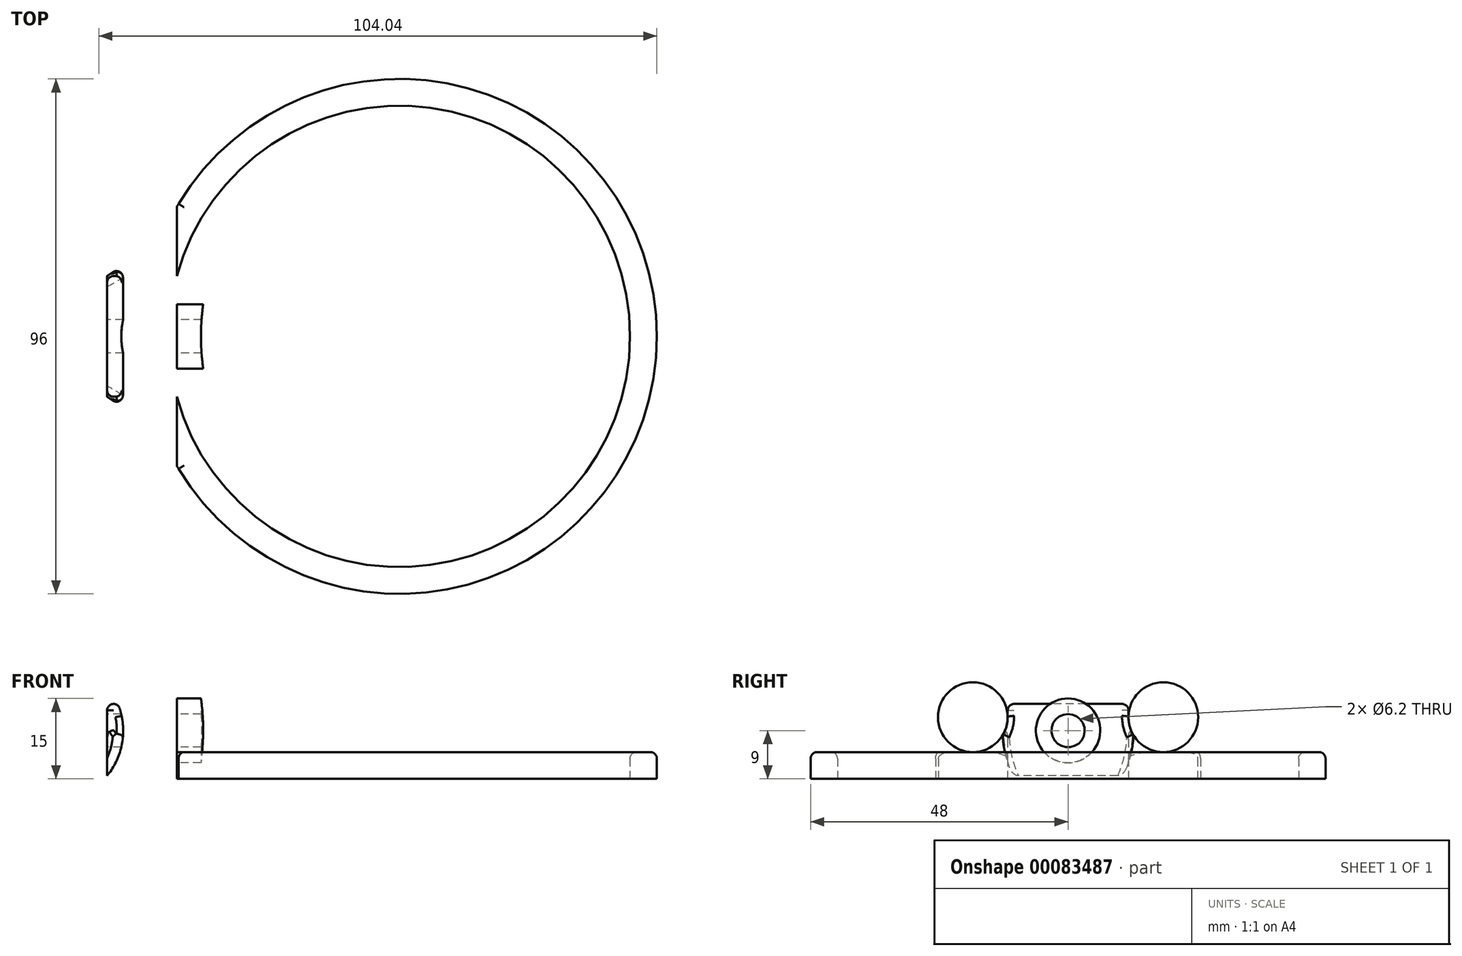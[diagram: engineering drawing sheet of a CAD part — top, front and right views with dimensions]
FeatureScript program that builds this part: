
annotation { "Feature Type Name" : "Feature", "Feature Type Description" : "" }
export const myFeature = defineFeature(function(context is Context, id is Id, definition is map)
    precondition{}
    {
        {
            var Q0;
            Q0=qCreatedBy(makeId("Top.planeOp"),FACE);
            var sketch = newSketch(context, id + "F0", { "sketchPlane" : qUnion([Q0])});
            skCircle(sketch, "E0", {"center": v(0, 0) * mm, "radius": 43 * mm});
            skCircle(sketch, "E1", {"center": v(0, 0) * mm, "radius": 48 * mm});
            skLineSegment(sketch, "E2.bottom", {"start": v(-41.5, -11.26) * mm, "end": v(-54.5, -11.26) * mm});
            skLineSegment(sketch, "E2.top", {"start": v(-41.5, 11.26) * mm, "end": v(-54.5, 11.26) * mm});
            skLineSegment(sketch, "E2.left", {"start": v(-41.5, -11.26) * mm, "end": v(-41.5, 11.26) * mm});
            skLineSegment(sketch, "E2.right", {"start": v(-54.5, -11.26) * mm, "end": v(-54.5, 11.26) * mm});
            skPoint(sketch, "E2.middle", {"position": v(-48, 0) * mm});
            skArc(sketch, "E3", {"start": v(-54.5, 11.26) * mm, "mid": v(-47.1, 17.26) * mm, "end": v(-41.16, 24.7) * mm});
            skArc(sketch, "E4.MirrorCS", {"start": v(-54.5, -11.26) * mm, "mid": v(-47.1, -17.26) * mm, "end": v(-41.16, -24.7) * mm});
            skSolve(sketch);
        }
        {
            var Q0;
            {var subQ0=sQuery(id+"F0.wireOp",EDGE,"E3");var subQ1=sQuery(id+"F0.wireOp",EDGE,"E1");var subQ8=makeQuery(id+"F0.imprint","INTERSECT",VERTEX,{"disambiguationData":[OD(1.0)],"derivedFrom":[subQ1,subQ0]});Q0=makeQuery(id+"F0.imprint","IMPRINT",FACE,{"disambiguationData":[TD([[makeQuery(id+"F0.imprint","IMPRINT",EDGE,{"disambiguationData":[TD([[subQ8,-1.0]])],"derivedFrom":subQ1}),1.0]])]});}
            var Q1;
            {var subQ4=sQuery(id+"F0.wireOp",EDGE,"E2.top");var subQ6=sQuery(id+"F0.wireOp",EDGE,"E1");var subQ7=makeQuery(id+"F0.imprint","INTERSECT",VERTEX,{"derivedFrom":[subQ6,subQ4]});Q1=makeQuery(id+"F0.imprint","IMPRINT",FACE,{"disambiguationData":[TD([[makeQuery(id+"F0.imprint","IMPRINT",EDGE,{"disambiguationData":[TD([[subQ7,-1.0]])],"derivedFrom":subQ6}),1.0]])]});}
            var Q2;
            {var subQ0=sQuery(id+"F0.wireOp",EDGE,"E3");var subQ1=sQuery(id+"F0.wireOp",EDGE,"E1");var subQ2=makeQuery(id+"F0.imprint","INTERSECT",VERTEX,{"disambiguationData":[OD(1.0)],"derivedFrom":[subQ1,subQ0]});Q2=makeQuery(id+"F0.imprint","IMPRINT",FACE,{"disambiguationData":[TD([[makeQuery(id+"F0.imprint","IMPRINT",EDGE,{"disambiguationData":[TD([[subQ2,-1.0]])],"derivedFrom":subQ1}),-1.0]])]});}
            var Q3;
            {var subQ5=sQuery(id+"F0.wireOp",EDGE,"E2.right");Q3=makeQuery(id+"F0.imprint","IMPRINT",FACE,{"disambiguationData":[TD([[makeQuery(id+"F0.imprint","IMPRINT",EDGE,{"derivedFrom":subQ5}),-1.0]])]});}
            var Q4;
            {var subQ0=sQuery(id+"F0.wireOp",EDGE,"E4.MirrorCS");var subQ1=sQuery(id+"F0.wireOp",EDGE,"E1");var subQ2=makeQuery(id+"F0.imprint","INTERSECT",VERTEX,{"disambiguationData":[OD(1.0)],"derivedFrom":[subQ1,subQ0]});Q4=makeQuery(id+"F0.imprint","IMPRINT",FACE,{"disambiguationData":[TD([[makeQuery(id+"F0.imprint","IMPRINT",EDGE,{"disambiguationData":[TD([[subQ2,1.0]])],"derivedFrom":subQ1}),-1.0]])]});}
            extrude(context, id + "F1", {"entities" : qUnion([Q0, Q1, Q2, Q3, Q4]), "depth" : 5 * mm});
        }
        {
            var Q0;
            {var subQ5=sQuery(id+"F0.wireOp",EDGE,"E2.right");Q0=makeQuery(id+"F0.imprint","IMPRINT",FACE,{"disambiguationData":[TD([[makeQuery(id+"F0.imprint","IMPRINT",EDGE,{"derivedFrom":subQ5}),-1.0]])]});}
            var Q1;
            {var subQ4=sQuery(id+"F0.wireOp",EDGE,"E2.top");var subQ6=sQuery(id+"F0.wireOp",EDGE,"E1");var subQ7=makeQuery(id+"F0.imprint","INTERSECT",VERTEX,{"derivedFrom":[subQ6,subQ4]});Q1=makeQuery(id+"F0.imprint","IMPRINT",FACE,{"disambiguationData":[TD([[makeQuery(id+"F0.imprint","IMPRINT",EDGE,{"disambiguationData":[TD([[subQ7,-1.0]])],"derivedFrom":subQ6}),1.0]])]});}
            extrude(context, id + "F2", {"entities" : qUnion([Q0, Q1]), "operationType" : NewBodyOperationType.ADD, "depth" : 18 * mm});
        }
        {
            var Q0;
            {var subQ0=sQuery(id+"F0.wireOp",EDGE,"E2.right");Q0=makeQuery(id+"F2.boolean.opBoolean","MERGE",FACE,{"derivedFrom":[makeQuery(id+"F1.opExtrude","SWEPT_FACE",FACE,{"disambiguationData":[OSD([subQ0])]}),makeQuery(id+"F2.opExtrude","SWEPT_FACE",FACE,{"disambiguationData":[OSD([subQ0])]})]});}
            var sketch = newSketch(context, id + "F3", { "sketchPlane" : qUnion([Q0])});
            skLineSegment(sketch, "E5", {"start": v(0, 18) * mm, "end": v(0, 0) * mm, "construction": true});
            skPoint(sketch, "E5.startSnap0", {"position": v(0, 18) * mm});
            skLineSegment(sketch, "E6.bottom", {"start": v(-11.26, 18) * mm, "end": v(11.26, 18) * mm});
            skLineSegment(sketch, "E6.top", {"start": v(-11.26, 0) * mm, "end": v(11.26, 0) * mm});
            skLineSegment(sketch, "E6.left", {"start": v(-11.26, 18) * mm, "end": v(-11.26, 0) * mm});
            skLineSegment(sketch, "E6.right", {"start": v(11.26, 18) * mm, "end": v(11.26, 0) * mm});
            skPoint(sketch, "E7", {"position": v(-11.26, 9) * mm});
            skCircle(sketch, "E8", {"center": v(0, 9) * mm, "radius": 6 * mm});
            skCircle(sketch, "E9", {"center": v(0, 9) * mm, "radius": 3.1 * mm});
            skSolve(sketch);
        }
        {
            var Q0;
            Q0=makeQuery(id+"F3.imprint","IMPRINT",FACE,{"disambiguationData":[TD([[makeQuery(id+"F3.imprint","IMPRINT",EDGE,{"derivedFrom":sQuery(id+"F3.wireOp",EDGE,"E9")}),1.0]])]});
            extrude(context, id + "F4", {"entities" : qUnion([Q0]), "operationType" : NewBodyOperationType.REMOVE, "endBound" : BoundingType.THROUGH_ALL, "oppositeDirection" : true, "depth" : 9.76 * mm});
        }
        {
            var Q0;
            Q0=makeQuery(id+"F3.imprint","IMPRINT",FACE,{"disambiguationData":[TD([[makeQuery(id+"F3.imprint","IMPRINT",EDGE,{"derivedFrom":sQuery(id+"F3.wireOp",EDGE,"E8")}),1.0]])]});
            var Q1;
            {var subQ0=sQuery(id+"F0.wireOp",EDGE,"E0");Q1=makeQuery(id+"F2.boolean.opBoolean","MERGE",FACE,{"derivedFrom":[makeQuery(id+"F1.opExtrude","SWEPT_FACE",FACE,{"disambiguationData":[OSD([subQ0])]}),makeQuery(id+"F2.opExtrude","SWEPT_FACE",FACE,{"disambiguationData":[OSD([subQ0])]})]});}
            extrude(context, id + "F5", {"entities" : qUnion([Q0]), "endBound" : BoundingType.UP_TO_SURFACE, "oppositeDirection" : true, "endBoundEntityFace" : qUnion([Q1]), "depth" : 15 * mm, "hasSecondDirectionDraft" : true, "secondDirectionDraftAngle" : 3 * degree});
        }
        {
            var Q0;
            Q0=makeQuery(id+"F5.opExtrude","SWEPT_BODY",BODY,{"disambiguationData":[OSD([sQuery(id+"F3.wireOp",EDGE,"E8"),sQuery(id+"F3.wireOp",EDGE,"E9")])]});
            transform(context, id + "F6", {"entities" : qUnion([Q0]), "transformType" : TransformType.TRANSLATION_3D, "dx" : 6 * mm, "dy" : 0 * mm, "dz" : 0 * mm, "makeCopy" : false});
        }
        {
            var Q0;
            Q0=makeQuery(id+"F5.opExtrude","SWEPT_BODY",BODY,{"disambiguationData":[OSD([sQuery(id+"F3.wireOp",EDGE,"E8"),sQuery(id+"F3.wireOp",EDGE,"E9")])]});
            var Q1;
            Q1=makeQuery(id+"F1.opExtrude","SWEPT_BODY",BODY,{"disambiguationData":[OSD([sQuery(id+"F0.wireOp",EDGE,"E0"),sQuery(id+"F0.wireOp",EDGE,"E1"),sQuery(id+"F0.wireOp",EDGE,"E2.right"),sQuery(id+"F0.wireOp",EDGE,"E3"),sQuery(id+"F0.wireOp",EDGE,"E4.MirrorCS")])]});
            booleanBodies(context, id + "F7", {"operationType" : BooleanOperationType.SUBTRACTION, "tools" : qUnion([Q0]), "targets" : qUnion([Q1]), "keepTools" : true});
        }
        {
            var Q0;
            Q0=makeQuery(id+"F2.opExtrude","SWEPT_FACE",FACE,{"disambiguationData":[OSD([sQuery(id+"F0.wireOp",EDGE,"E2.bottom")])]});
            var sketch = newSketch(context, id + "F8", { "sketchPlane" : qUnion([Q0])});
            skLineSegment(sketch, "E10.bottom", {"start": v(-54.5, 18) * mm, "end": v(-41.5, 18) * mm});
            skLineSegment(sketch, "E10.top", {"start": v(-54.5, 0) * mm, "end": v(-41.5, 0) * mm});
            skLineSegment(sketch, "E10.left", {"start": v(-54.5, 18) * mm, "end": v(-54.5, 0) * mm});
            skLineSegment(sketch, "E10.right", {"start": v(-41.5, 18) * mm, "end": v(-41.5, 0) * mm});
            skCircle(sketch, "E11", {"center": v(-64.85, 9) * mm, "radius": 13.35 * mm});
            skPoint(sketch, "E12", {"position": v(-54.5, 9) * mm});
            skLineSegment(sketch, "E13.0.0", {"start": v(-48.5, 15) * mm, "end": v(-48.5, 3) * mm});
            skSolve(sketch);
        }
        {
            var Q0;
            {var subQ0=sQuery(id+"F8.wireOp",EDGE,"E10.left");var subQ3=sQuery(id+"F8.wireOp",EDGE,"E11");var subQ4=makeQuery(id+"F8.imprint","INTERSECT",VERTEX,{"disambiguationData":[OD(0.0)],"derivedFrom":[subQ0,subQ3]});Q0=makeQuery(id+"F8.imprint","IMPRINT",FACE,{"disambiguationData":[TD([[makeQuery(id+"F8.imprint","IMPRINT",EDGE,{"disambiguationData":[TD([[subQ4,-1.0]])],"derivedFrom":subQ0}),1.0]])]});}
            var Q1;
            {var subQ0=sQuery(id+"F8.wireOp",EDGE,"E10.left");var subQ3=sQuery(id+"F8.wireOp",EDGE,"E11");var subQ4=makeQuery(id+"F8.imprint","INTERSECT",VERTEX,{"disambiguationData":[OD(1.0)],"derivedFrom":[subQ0,subQ3]});Q1=makeQuery(id+"F8.imprint","IMPRINT",FACE,{"disambiguationData":[TD([[makeQuery(id+"F8.imprint","IMPRINT",EDGE,{"disambiguationData":[TD([[subQ4,1.0]])],"derivedFrom":subQ0}),1.0]])]});}
            var Q2;
            Q2=sQuery(id+"F8.wireOp",EDGE,"E11");
            extrude(context, id + "F9", {"entities" : qUnion([Q0, Q1]), "operationType" : NewBodyOperationType.REMOVE, "surfaceEntities" : qUnion([Q2]), "endBound" : BoundingType.THROUGH_ALL, "oppositeDirection" : true, "depth" : 25 * mm, "hasSecondDirection" : true, "secondDirectionBound" : SecondDirectionBoundingType.THROUGH_ALL, "secondDirectionOppositeDirection" : false, "secondDirectionDepth" : 25 * mm});
        }
        {
            var Q0;
            Q0=makeQuery(id+"F2.boolean.opBoolean","INTERSECT",EDGE,{"derivedFrom":[makeQuery(id+"F1.opExtrude","CAP_FACE",FACE,{"disambiguationData":[OSD([sQuery(id+"F0.wireOp",EDGE,"E0"),sQuery(id+"F0.wireOp",EDGE,"E1"),sQuery(id+"F0.wireOp",EDGE,"E2.right"),sQuery(id+"F0.wireOp",EDGE,"E3"),sQuery(id+"F0.wireOp",EDGE,"E4.MirrorCS")])],"isStart":false}),makeQuery(id+"F2.opExtrude","SWEPT_FACE",FACE,{"disambiguationData":[OSD([sQuery(id+"F0.wireOp",EDGE,"E2.bottom")])]})]});
            var Q1;
            Q1=makeQuery(id+"F2.opExtrude","CAP_EDGE",EDGE,{"disambiguationData":[OSD([sQuery(id+"F0.wireOp",EDGE,"E2.bottom")])],"isStart":false});
            var Q2;
            Q2=makeQuery(id+"F2.boolean.opBoolean","INTERSECT",EDGE,{"derivedFrom":[makeQuery(id+"F1.opExtrude","CAP_FACE",FACE,{"disambiguationData":[OSD([sQuery(id+"F0.wireOp",EDGE,"E0"),sQuery(id+"F0.wireOp",EDGE,"E1"),sQuery(id+"F0.wireOp",EDGE,"E2.right"),sQuery(id+"F0.wireOp",EDGE,"E3"),sQuery(id+"F0.wireOp",EDGE,"E4.MirrorCS")])],"isStart":false}),makeQuery(id+"F2.opExtrude","SWEPT_FACE",FACE,{"disambiguationData":[OSD([sQuery(id+"F0.wireOp",EDGE,"E2.top")])]})]});
            var Q3;
            Q3=makeQuery(id+"F2.opExtrude","CAP_EDGE",EDGE,{"disambiguationData":[OSD([sQuery(id+"F0.wireOp",EDGE,"E2.top")])],"isStart":false});
            fillet(context, id + "F10", {"entities" : qUnion([Q0, Q1, Q2, Q3]), "radius" : 6.5 * mm, "tangentPropagation" : true, "allowEdgeOverflow" : false});
        }
        {
            var Q0;
            Q0=makeQuery(id+"F1.opExtrude","CAP_EDGE",EDGE,{"disambiguationData":[OSD([sQuery(id+"F0.wireOp",EDGE,"E0")])],"isStart":false});
            var Q1;
            Q1=makeQuery(id+"F1.opExtrude","CAP_EDGE",EDGE,{"disambiguationData":[OSD([sQuery(id+"F0.wireOp",EDGE,"E1")])],"isStart":false});
            var Q2;
            Q2=makeQuery(id+"F1.opExtrude","CAP_EDGE",EDGE,{"disambiguationData":[OSD([sQuery(id+"F0.wireOp",EDGE,"E4.MirrorCS")])],"isStart":false});
            var Q3;
            {var subQ0=sQuery(id+"F0.wireOp",EDGE,"E4.MirrorCS");Q3=makeQuery(id+"F10.opFillet","BLEND_EDGE",EDGE,{"blendedFrom":[makeQuery(id+"F2.boolean.opBoolean","INTERSECT",EDGE,{"derivedFrom":[makeQuery(id+"F1.opExtrude","CAP_FACE",FACE,{"disambiguationData":[OSD([sQuery(id+"F0.wireOp",EDGE,"E0"),sQuery(id+"F0.wireOp",EDGE,"E1"),sQuery(id+"F0.wireOp",EDGE,"E2.right"),sQuery(id+"F0.wireOp",EDGE,"E3"),subQ0])],"isStart":false}),makeQuery(id+"F2.opExtrude","SWEPT_FACE",FACE,{"disambiguationData":[OSD([sQuery(id+"F0.wireOp",EDGE,"E2.bottom")])]})]}),makeQuery(id+"F1.opExtrude","SWEPT_FACE",FACE,{"disambiguationData":[OSD([subQ0])]})],"blendedInto":[makeQuery(id+"F1.opExtrude","SWEPT_FACE",FACE,{"disambiguationData":[OSD([subQ0])]})]});}
            var Q4;
            {var subQ0=sQuery(id+"F0.wireOp",EDGE,"E0");Q4=makeQuery(id+"F10.opFillet","BLEND_EDGE",EDGE,{"blendedFrom":[makeQuery(id+"F2.boolean.opBoolean","INTERSECT",EDGE,{"derivedFrom":[makeQuery(id+"F1.opExtrude","CAP_FACE",FACE,{"disambiguationData":[OSD([subQ0,sQuery(id+"F0.wireOp",EDGE,"E1"),sQuery(id+"F0.wireOp",EDGE,"E2.right"),sQuery(id+"F0.wireOp",EDGE,"E3"),sQuery(id+"F0.wireOp",EDGE,"E4.MirrorCS")])],"isStart":false}),makeQuery(id+"F2.opExtrude","SWEPT_FACE",FACE,{"disambiguationData":[OSD([sQuery(id+"F0.wireOp",EDGE,"E2.bottom")])]})]}),makeQuery(id+"F2.boolean.opBoolean","MERGE",FACE,{"derivedFrom":[makeQuery(id+"F1.opExtrude","SWEPT_FACE",FACE,{"disambiguationData":[OSD([subQ0])]}),makeQuery(id+"F2.opExtrude","SWEPT_FACE",FACE,{"disambiguationData":[OSD([subQ0])]})]})],"blendedInto":[makeQuery(id+"F2.boolean.opBoolean","MERGE",FACE,{"derivedFrom":[makeQuery(id+"F1.opExtrude","SWEPT_FACE",FACE,{"disambiguationData":[OSD([subQ0])]}),makeQuery(id+"F2.opExtrude","SWEPT_FACE",FACE,{"disambiguationData":[OSD([subQ0])]})]})]});}
            var Q5;
            {var subQ0=sQuery(id+"F0.wireOp",EDGE,"E0");Q5=makeQuery(id+"F10.opFillet","BLEND_EDGE",EDGE,{"blendedFrom":[makeQuery(id+"F2.opExtrude","CAP_EDGE",EDGE,{"disambiguationData":[OSD([sQuery(id+"F0.wireOp",EDGE,"E2.bottom")])],"isStart":false}),makeQuery(id+"F2.boolean.opBoolean","MERGE",FACE,{"derivedFrom":[makeQuery(id+"F1.opExtrude","SWEPT_FACE",FACE,{"disambiguationData":[OSD([subQ0])]}),makeQuery(id+"F2.opExtrude","SWEPT_FACE",FACE,{"disambiguationData":[OSD([subQ0])]})]})],"blendedInto":[makeQuery(id+"F2.boolean.opBoolean","MERGE",FACE,{"derivedFrom":[makeQuery(id+"F1.opExtrude","SWEPT_FACE",FACE,{"disambiguationData":[OSD([subQ0])]}),makeQuery(id+"F2.opExtrude","SWEPT_FACE",FACE,{"disambiguationData":[OSD([subQ0])]})]})]});}
            var Q6;
            Q6=makeQuery(id+"F2.opExtrude","CAP_EDGE",EDGE,{"disambiguationData":[OSD([sQuery(id+"F0.wireOp",EDGE,"E0")])],"isStart":false});
            var Q7;
            {var subQ0=sQuery(id+"F0.wireOp",EDGE,"E0");Q7=makeQuery(id+"F10.opFillet","BLEND_EDGE",EDGE,{"blendedFrom":[makeQuery(id+"F2.opExtrude","CAP_EDGE",EDGE,{"disambiguationData":[OSD([sQuery(id+"F0.wireOp",EDGE,"E2.top")])],"isStart":false}),makeQuery(id+"F2.boolean.opBoolean","MERGE",FACE,{"derivedFrom":[makeQuery(id+"F1.opExtrude","SWEPT_FACE",FACE,{"disambiguationData":[OSD([subQ0])]}),makeQuery(id+"F2.opExtrude","SWEPT_FACE",FACE,{"disambiguationData":[OSD([subQ0])]})]})],"blendedInto":[makeQuery(id+"F2.boolean.opBoolean","MERGE",FACE,{"derivedFrom":[makeQuery(id+"F1.opExtrude","SWEPT_FACE",FACE,{"disambiguationData":[OSD([subQ0])]}),makeQuery(id+"F2.opExtrude","SWEPT_FACE",FACE,{"disambiguationData":[OSD([subQ0])]})]})]});}
            var Q8;
            {var subQ0=sQuery(id+"F0.wireOp",EDGE,"E0");Q8=makeQuery(id+"F10.opFillet","BLEND_EDGE",EDGE,{"blendedFrom":[makeQuery(id+"F2.boolean.opBoolean","INTERSECT",EDGE,{"derivedFrom":[makeQuery(id+"F1.opExtrude","CAP_FACE",FACE,{"disambiguationData":[OSD([subQ0,sQuery(id+"F0.wireOp",EDGE,"E1"),sQuery(id+"F0.wireOp",EDGE,"E2.right"),sQuery(id+"F0.wireOp",EDGE,"E3"),sQuery(id+"F0.wireOp",EDGE,"E4.MirrorCS")])],"isStart":false}),makeQuery(id+"F2.opExtrude","SWEPT_FACE",FACE,{"disambiguationData":[OSD([sQuery(id+"F0.wireOp",EDGE,"E2.top")])]})]}),makeQuery(id+"F2.boolean.opBoolean","MERGE",FACE,{"derivedFrom":[makeQuery(id+"F1.opExtrude","SWEPT_FACE",FACE,{"disambiguationData":[OSD([subQ0])]}),makeQuery(id+"F2.opExtrude","SWEPT_FACE",FACE,{"disambiguationData":[OSD([subQ0])]})]})],"blendedInto":[makeQuery(id+"F2.boolean.opBoolean","MERGE",FACE,{"derivedFrom":[makeQuery(id+"F1.opExtrude","SWEPT_FACE",FACE,{"disambiguationData":[OSD([subQ0])]}),makeQuery(id+"F2.opExtrude","SWEPT_FACE",FACE,{"disambiguationData":[OSD([subQ0])]})]})]});}
            var Q9;
            Q9=makeQuery(id+"F2.opExtrude","SWEPT_EDGE",EDGE,{"disambiguationData":[OSD([sQuery(id+"F0.wireOp",EDGE,"E0"),sQuery(id+"F0.wireOp",EDGE,"E2.bottom"),sQuery(id+"F0.wireOp",EDGE,"E2.left")])]});
            var Q10;
            Q10=makeQuery(id+"F2.opExtrude","SWEPT_EDGE",EDGE,{"disambiguationData":[OSD([sQuery(id+"F0.wireOp",EDGE,"E0"),sQuery(id+"F0.wireOp",EDGE,"E2.top"),sQuery(id+"F0.wireOp",EDGE,"E2.left")])]});
            var Q11;
            Q11=makeQuery(id+"F1.opExtrude","CAP_EDGE",EDGE,{"disambiguationData":[OSD([sQuery(id+"F0.wireOp",EDGE,"E3")])],"isStart":false});
            var Q12;
            {var subQ0=sQuery(id+"F0.wireOp",EDGE,"E3");Q12=makeQuery(id+"F10.opFillet","BLEND_EDGE",EDGE,{"blendedFrom":[makeQuery(id+"F2.boolean.opBoolean","INTERSECT",EDGE,{"derivedFrom":[makeQuery(id+"F1.opExtrude","CAP_FACE",FACE,{"disambiguationData":[OSD([sQuery(id+"F0.wireOp",EDGE,"E0"),sQuery(id+"F0.wireOp",EDGE,"E1"),sQuery(id+"F0.wireOp",EDGE,"E2.right"),subQ0,sQuery(id+"F0.wireOp",EDGE,"E4.MirrorCS")])],"isStart":false}),makeQuery(id+"F2.opExtrude","SWEPT_FACE",FACE,{"disambiguationData":[OSD([sQuery(id+"F0.wireOp",EDGE,"E2.top")])]})]}),makeQuery(id+"F1.opExtrude","SWEPT_FACE",FACE,{"disambiguationData":[OSD([subQ0])]})],"blendedInto":[makeQuery(id+"F1.opExtrude","SWEPT_FACE",FACE,{"disambiguationData":[OSD([subQ0])]})]});}
            fillet(context, id + "F11", {"entities" : qUnion([Q0, Q1, Q2, Q3, Q4, Q5, Q6, Q7, Q8, Q9, Q10, Q11, Q12]), "radius" : 1.2 * mm, "tangentPropagation" : true, "allowEdgeOverflow" : false});
        }
        {
            var Q0;
            Q0=makeQuery(id+"F1.opExtrude","CAP_EDGE",EDGE,{"disambiguationData":[OSD([sQuery(id+"F0.wireOp",EDGE,"E4.MirrorCS")])],"isStart":true});
            var Q1;
            Q1=makeQuery(id+"F1.opExtrude","CAP_EDGE",EDGE,{"disambiguationData":[OSD([sQuery(id+"F0.wireOp",EDGE,"E2.right")])],"isStart":true});
            var Q2;
            Q2=makeQuery(id+"F1.opExtrude","CAP_EDGE",EDGE,{"disambiguationData":[OSD([sQuery(id+"F0.wireOp",EDGE,"E3")])],"isStart":true});
            var Q3;
            Q3=makeQuery(id+"F2.opExtrude","CAP_EDGE",EDGE,{"disambiguationData":[OSD([sQuery(id+"F0.wireOp",EDGE,"E2.right")])],"isStart":false});
            var Q4;
            Q4=makeQuery(id+"F10.opFillet","BLEND_EDGE",EDGE,{"blendedFrom":[makeQuery(id+"F2.boolean.opBoolean","INTERSECT",EDGE,{"derivedFrom":[makeQuery(id+"F1.opExtrude","CAP_FACE",FACE,{"disambiguationData":[OSD([sQuery(id+"F0.wireOp",EDGE,"E0"),sQuery(id+"F0.wireOp",EDGE,"E1"),sQuery(id+"F0.wireOp",EDGE,"E2.right"),sQuery(id+"F0.wireOp",EDGE,"E3"),sQuery(id+"F0.wireOp",EDGE,"E4.MirrorCS")])],"isStart":false}),makeQuery(id+"F2.opExtrude","SWEPT_FACE",FACE,{"disambiguationData":[OSD([sQuery(id+"F0.wireOp",EDGE,"E2.bottom")])]})]}),makeQuery(id+"F9.boolean.opBoolean","COPY",FACE,{"derivedFrom":makeQuery(id+"F9.opExtrude","SWEPT_FACE",FACE,{"disambiguationData":[OSD([sQuery(id+"F8.wireOp",EDGE,"E11")])]})})],"blendedInto":[makeQuery(id+"F9.boolean.opBoolean","COPY",FACE,{"derivedFrom":makeQuery(id+"F9.opExtrude","SWEPT_FACE",FACE,{"disambiguationData":[OSD([sQuery(id+"F8.wireOp",EDGE,"E11")])]})})]});
            var Q5;
            Q5=makeQuery(id+"F9.boolean.opBoolean","INTERSECT",EDGE,{"derivedFrom":[makeQuery(id+"F1.opExtrude","SWEPT_FACE",FACE,{"disambiguationData":[OSD([sQuery(id+"F0.wireOp",EDGE,"E3")])]}),makeQuery(id+"F9.opExtrude","SWEPT_FACE",FACE,{"disambiguationData":[OSD([sQuery(id+"F8.wireOp",EDGE,"E11")])]})]});
            var Q6;
            Q6=makeQuery(id+"F10.opFillet","BLEND_EDGE",EDGE,{"blendedFrom":[makeQuery(id+"F2.opExtrude","CAP_EDGE",EDGE,{"disambiguationData":[OSD([sQuery(id+"F0.wireOp",EDGE,"E2.top")])],"isStart":false}),makeQuery(id+"F9.boolean.opBoolean","COPY",FACE,{"derivedFrom":makeQuery(id+"F9.opExtrude","SWEPT_FACE",FACE,{"disambiguationData":[OSD([sQuery(id+"F8.wireOp",EDGE,"E11")])]})})],"blendedInto":[makeQuery(id+"F9.boolean.opBoolean","COPY",FACE,{"derivedFrom":makeQuery(id+"F9.opExtrude","SWEPT_FACE",FACE,{"disambiguationData":[OSD([sQuery(id+"F8.wireOp",EDGE,"E11")])]})})]});
            var Q7;
            Q7=makeQuery(id+"F10.opFillet","BLEND_EDGE",EDGE,{"blendedFrom":[makeQuery(id+"F2.boolean.opBoolean","INTERSECT",EDGE,{"derivedFrom":[makeQuery(id+"F1.opExtrude","CAP_FACE",FACE,{"disambiguationData":[OSD([sQuery(id+"F0.wireOp",EDGE,"E0"),sQuery(id+"F0.wireOp",EDGE,"E1"),sQuery(id+"F0.wireOp",EDGE,"E2.right"),sQuery(id+"F0.wireOp",EDGE,"E3"),sQuery(id+"F0.wireOp",EDGE,"E4.MirrorCS")])],"isStart":false}),makeQuery(id+"F2.opExtrude","SWEPT_FACE",FACE,{"disambiguationData":[OSD([sQuery(id+"F0.wireOp",EDGE,"E2.top")])]})]}),makeQuery(id+"F9.boolean.opBoolean","COPY",FACE,{"derivedFrom":makeQuery(id+"F9.opExtrude","SWEPT_FACE",FACE,{"disambiguationData":[OSD([sQuery(id+"F8.wireOp",EDGE,"E11")])]})})],"blendedInto":[makeQuery(id+"F9.boolean.opBoolean","COPY",FACE,{"derivedFrom":makeQuery(id+"F9.opExtrude","SWEPT_FACE",FACE,{"disambiguationData":[OSD([sQuery(id+"F8.wireOp",EDGE,"E11")])]})})]});
            var Q8;
            Q8=makeQuery(id+"F10.opFillet","BLEND_EDGE",EDGE,{"blendedFrom":[makeQuery(id+"F2.opExtrude","CAP_EDGE",EDGE,{"disambiguationData":[OSD([sQuery(id+"F0.wireOp",EDGE,"E2.bottom")])],"isStart":false}),makeQuery(id+"F9.boolean.opBoolean","COPY",FACE,{"derivedFrom":makeQuery(id+"F9.opExtrude","SWEPT_FACE",FACE,{"disambiguationData":[OSD([sQuery(id+"F8.wireOp",EDGE,"E11")])]})})],"blendedInto":[makeQuery(id+"F9.boolean.opBoolean","COPY",FACE,{"derivedFrom":makeQuery(id+"F9.opExtrude","SWEPT_FACE",FACE,{"disambiguationData":[OSD([sQuery(id+"F8.wireOp",EDGE,"E11")])]})})]});
            fillet(context, id + "F12", {"entities" : qUnion([Q0, Q1, Q2, Q3, Q4, Q5, Q6, Q7, Q8]), "radius" : 1.2 * mm, "tangentPropagation" : true, "allowEdgeOverflow" : false});
        }
    });
